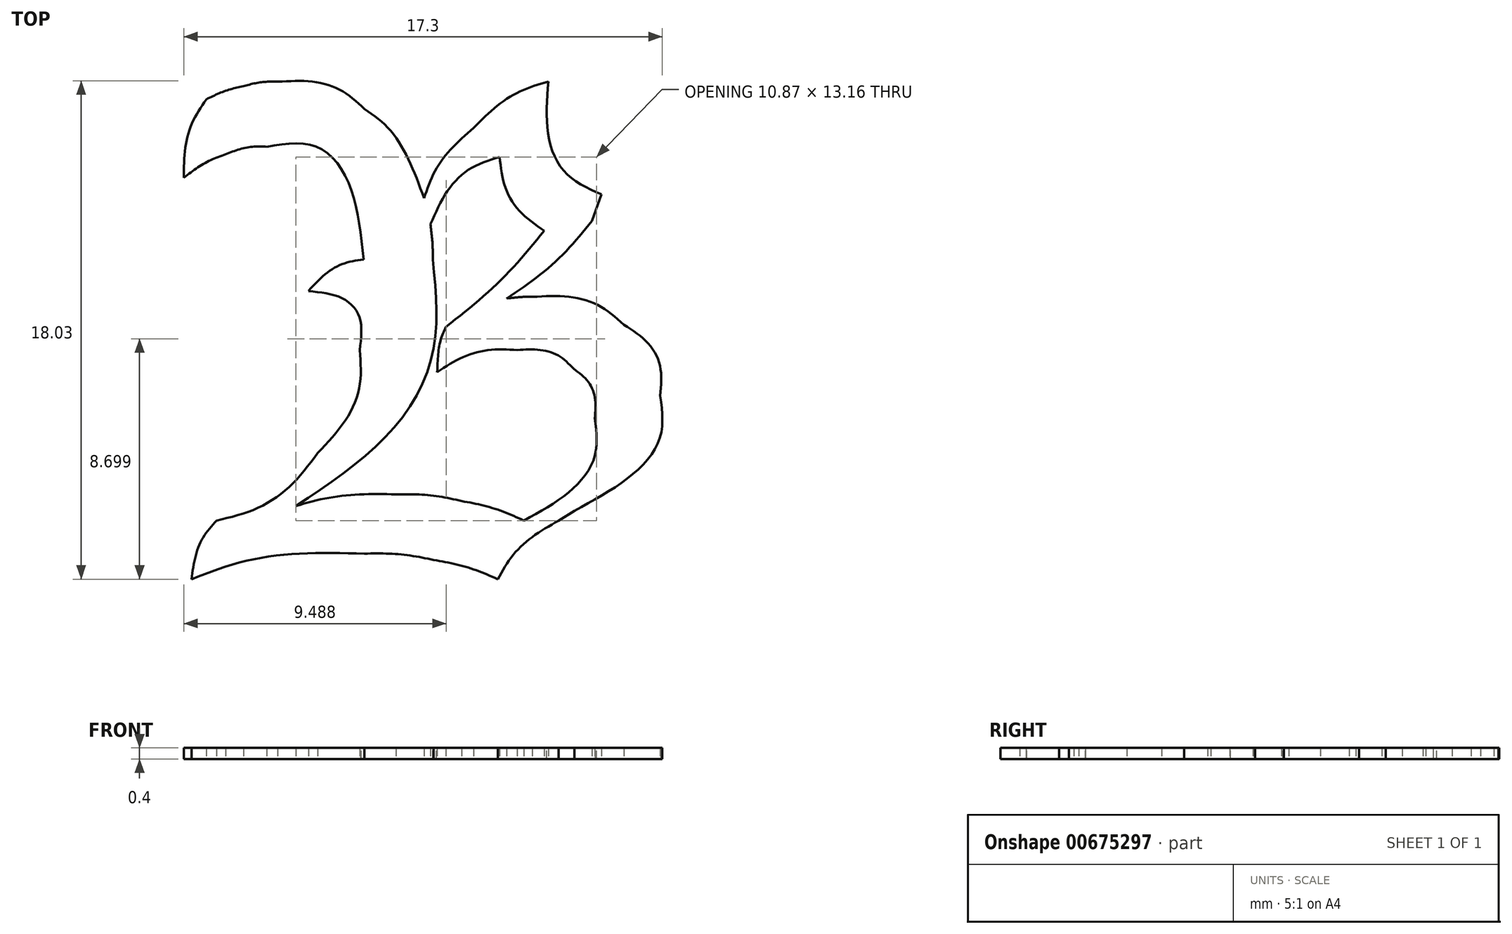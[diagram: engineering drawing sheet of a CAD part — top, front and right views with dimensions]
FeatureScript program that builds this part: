
annotation { "Feature Type Name" : "Feature", "Feature Type Description" : "" }
export const myFeature = defineFeature(function(context is Context, id is Id, definition is map)
    precondition{}
    {
        {
            var Q0;
            Q0=qCreatedBy(makeId("Top.planeOp"),FACE);
            var sketch = newSketch(context, id + "F0", { "sketchPlane" : qUnion([Q0])});
            skFitSpline(sketch, "E0", {"points": [v(-41.57, -9) * mm, v(-41.42, -8.14) * mm, v(-41.12, -7.43) * mm, v(-40.67, -6.88) * mm]});
            skFitSpline(sketch, "E1", {"points": [v(-40.67, -6.88) * mm, v(-39.23, -6.45) * mm, v(-38.01, -5.63) * mm, v(-37, -4.44) * mm]});
            skFitSpline(sketch, "E2", {"points": [v(-37, -4.44) * mm, v(-36, -3.23) * mm, v(-35.49, -1.99) * mm, v(-35.49, -0.7) * mm]});
            skFitSpline(sketch, "E3", {"points": [v(-35.49, -0.7) * mm, v(-35.49, 0.45) * mm, v(-36.1, 1.16) * mm, v(-37.34, 1.42) * mm]});
            skFitSpline(sketch, "E4", {"points": [v(-37.34, 1.42) * mm, v(-36.74, 2.03) * mm, v(-36.08, 2.42) * mm, v(-35.35, 2.57) * mm]});
            skFitSpline(sketch, "E5", {"points": [v(-35.35, 2.57) * mm, v(-35.88, 5.29) * mm, v(-37.04, 6.65) * mm, v(-38.85, 6.65) * mm]});
            skFitSpline(sketch, "E6", {"points": [v(-38.85, 6.65) * mm, v(-39.34, 6.65) * mm, v(-39.84, 6.56) * mm, v(-40.33, 6.37) * mm]});
            skFitSpline(sketch, "E7", {"points": [v(-40.33, 6.37) * mm, v(-40.83, 6.19) * mm, v(-41.34, 5.9) * mm, v(-41.85, 5.53) * mm]});
            skFitSpline(sketch, "E8", {"points": [v(-41.85, 5.53) * mm, v(-41.8, 6.6) * mm, v(-41.52, 7.55) * mm, v(-41.04, 8.36) * mm]});
            skFitSpline(sketch, "E9", {"points": [v(-41.04, 8.36) * mm, v(-40.57, 8.58) * mm, v(-40.13, 8.74) * mm, v(-39.7, 8.84) * mm]});
            skFitSpline(sketch, "E10", {"points": [v(-39.7, 8.84) * mm, v(-39.26, 8.95) * mm, v(-38.85, 9) * mm, v(-38.46, 9) * mm]});
            skFitSpline(sketch, "E11", {"points": [v(-38.46, 9) * mm, v(-37.19, 9) * mm, v(-36.14, 8.67) * mm, v(-35.32, 8.02) * mm]});
            skFitSpline(sketch, "E12", {"points": [v(-35.32, 8.02) * mm, v(-34.49, 7.36) * mm, v(-33.77, 6.28) * mm, v(-33.16, 4.78) * mm]});
            skFitSpline(sketch, "E13", {"points": [v(-33.16, 4.78) * mm, v(-32.8, 5.7) * mm, v(-32.2, 6.54) * mm, v(-31.37, 7.33) * mm]});
            skFitSpline(sketch, "E14", {"points": [v(-31.37, 7.33) * mm, v(-30.52, 8.13) * mm, v(-29.62, 8.68) * mm, v(-28.67, 9) * mm]});
            skFitSpline(sketch, "E15", {"points": [v(-28.67, 9) * mm, v(-28.67, 7.05) * mm, v(-28.03, 5.69) * mm, v(-26.74, 4.92) * mm]});
            skLineSegment(sketch, "E16", {"start": v(-26.74, 4.92) * mm, "end": v(-27.1, 3.96) * mm});
            skFitSpline(sketch, "E17", {"points": [v(-27.1, 3.96) * mm, v(-27.96, 2.93) * mm, v(-29, 2) * mm, v(-30.17, 1.16) * mm]});
            skFitSpline(sketch, "E18", {"points": [v(-30.17, 1.16) * mm, v(-29.81, 1.2) * mm, v(-29.5, 1.22) * mm, v(-29.25, 1.22) * mm]});
            skFitSpline(sketch, "E19", {"points": [v(-29.25, 1.22) * mm, v(-27.9, 1.22) * mm, v(-26.8, 0.88) * mm, v(-25.93, 0.2) * mm]});
            skFitSpline(sketch, "E20", {"points": [v(-25.93, 0.2) * mm, v(-25.06, -0.46) * mm, v(-24.63, -1.32) * mm, v(-24.63, -2.36) * mm]});
            skFitSpline(sketch, "E21", {"points": [v(-24.63, -2.36) * mm, v(-24.63, -3.85) * mm, v(-25.66, -5.24) * mm, v(-27.73, -6.52) * mm]});
            skLineSegment(sketch, "E22", {"start": v(-27.73, -6.52) * mm, "end": v(-28.3, -6.88) * mm});
            skFitSpline(sketch, "E23", {"points": [v(-28.3, -6.88) * mm, v(-29.25, -7.47) * mm, v(-29.99, -8.18) * mm, v(-30.5, -9) * mm]});
            skFitSpline(sketch, "E24", {"points": [v(-30.5, -9) * mm, v(-31.24, -8.7) * mm, v(-32.01, -8.46) * mm, v(-32.81, -8.3) * mm]});
            skFitSpline(sketch, "E25", {"points": [v(-32.81, -8.3) * mm, v(-33.62, -8.15) * mm, v(-34.45, -8.07) * mm, v(-35.32, -8.07) * mm]});
            skFitSpline(sketch, "E26", {"points": [v(-35.32, -8.07) * mm, v(-37.7, -8.07) * mm, v(-39.79, -8.38) * mm, v(-41.57, -9) * mm]});
            skLineSegment(sketch, "E27", {"start": v(-41.57, -9) * mm, "end": v(-41.57, -9) * mm});
            skFitSpline(sketch, "E28", {"points": [v(-37.8, -6.35) * mm, v(-36.7, -6.07) * mm, v(-35.49, -5.93) * mm, v(-34.18, -5.93) * mm]});
            skFitSpline(sketch, "E29", {"points": [v(-34.18, -5.93) * mm, v(-33.37, -5.93) * mm, v(-32.58, -6.01) * mm, v(-31.8, -6.17) * mm]});
            skFitSpline(sketch, "E30", {"points": [v(-31.8, -6.17) * mm, v(-31.03, -6.33) * mm, v(-30.28, -6.56) * mm, v(-29.55, -6.88) * mm]});
            skFitSpline(sketch, "E31", {"points": [v(-29.55, -6.88) * mm, v(-27.84, -5.78) * mm, v(-26.99, -4.54) * mm, v(-26.99, -3.17) * mm]});
            skFitSpline(sketch, "E32", {"points": [v(-26.99, -3.17) * mm, v(-26.99, -2.43) * mm, v(-27.24, -1.84) * mm, v(-27.75, -1.39) * mm]});
            skFitSpline(sketch, "E33", {"points": [v(-27.75, -1.39) * mm, v(-28.26, -0.93) * mm, v(-28.94, -0.7) * mm, v(-29.8, -0.7) * mm]});
            skFitSpline(sketch, "E34", {"points": [v(-29.8, -0.7) * mm, v(-30.81, -0.7) * mm, v(-31.78, -0.97) * mm, v(-32.69, -1.5) * mm]});
            skFitSpline(sketch, "E35", {"points": [v(-32.69, -1.5) * mm, v(-32.65, -0.83) * mm, v(-32.54, -0.28) * mm, v(-32.37, 0.13) * mm]});
            skFitSpline(sketch, "E36", {"points": [v(-32.37, 0.13) * mm, v(-31.05, 1.2) * mm, v(-29.86, 2.37) * mm, v(-28.82, 3.6) * mm]});
            skFitSpline(sketch, "E37", {"points": [v(-28.82, 3.6) * mm, v(-29.7, 4.31) * mm, v(-30.24, 5.2) * mm, v(-30.43, 6.28) * mm]});
            skFitSpline(sketch, "E38", {"points": [v(-30.43, 6.28) * mm, v(-31.48, 5.86) * mm, v(-32.31, 5.05) * mm, v(-32.93, 3.85) * mm]});
            skFitSpline(sketch, "E39", {"points": [v(-32.93, 3.85) * mm, v(-32.88, 3.36) * mm, v(-32.85, 2.93) * mm, v(-32.85, 2.57) * mm]});
            skFitSpline(sketch, "E40", {"points": [v(-32.85, 2.57) * mm, v(-32.85, -0.82) * mm, v(-34.5, -3.8) * mm, v(-37.8, -6.35) * mm]});
            skFitSpline(sketch, "E41", {"points": [v(-23.24, -4.97) * mm, v(-23.24, -5.33) * mm, v(-23.18, -5.74) * mm, v(-23.07, -6.2) * mm]});
            skFitSpline(sketch, "E42", {"points": [v(-23.07, -6.2) * mm, v(-22.94, -6.64) * mm, v(-22.77, -7.06) * mm, v(-22.55, -7.46) * mm]});
            skFitSpline(sketch, "E43", {"points": [v(-22.55, -7.46) * mm, v(-22.31, -7.85) * mm, v(-22.03, -8.18) * mm, v(-21.72, -8.45) * mm]});
            skFitSpline(sketch, "E44", {"points": [v(-21.72, -8.45) * mm, v(-21.4, -8.72) * mm, v(-21.05, -8.86) * mm, v(-20.65, -8.86) * mm]});
            skFitSpline(sketch, "E45", {"points": [v(-20.65, -8.86) * mm, v(-20.16, -8.86) * mm, v(-19.64, -8.73) * mm, v(-19.08, -8.48) * mm]});
            skFitSpline(sketch, "E46", {"points": [v(-19.08, -8.48) * mm, v(-18.53, -8.22) * mm, v(-18.03, -7.95) * mm, v(-17.59, -7.65) * mm]});
            skFitSpline(sketch, "E47", {"points": [v(-17.59, -7.65) * mm, v(-17.13, -7.35) * mm, v(-16.78, -7.08) * mm, v(-16.52, -6.84) * mm]});
            skFitSpline(sketch, "E48", {"points": [v(-16.52, -6.84) * mm, v(-16.25, -6.59) * mm, v(-16.17, -6.48) * mm, v(-16.26, -6.5) * mm]});
            skFitSpline(sketch, "E49", {"points": [v(-16.26, -6.5) * mm, v(-16.37, -6.54) * mm, v(-16.53, -6.62) * mm, v(-16.74, -6.74) * mm]});
            skFitSpline(sketch, "E50", {"points": [v(-16.74, -6.74) * mm, v(-16.94, -6.87) * mm, v(-17.16, -7) * mm, v(-17.4, -7.15) * mm]});
            skFitSpline(sketch, "E51", {"points": [v(-17.4, -7.15) * mm, v(-17.64, -7.3) * mm, v(-17.87, -7.42) * mm, v(-18.11, -7.53) * mm]});
            skFitSpline(sketch, "E52", {"points": [v(-18.11, -7.53) * mm, v(-18.35, -7.64) * mm, v(-18.56, -7.7) * mm, v(-18.75, -7.7) * mm]});
            skFitSpline(sketch, "E53", {"points": [v(-18.75, -7.7) * mm, v(-19.08, -7.7) * mm, v(-19.38, -7.58) * mm, v(-19.65, -7.34) * mm]});
            skFitSpline(sketch, "E54", {"points": [v(-19.65, -7.34) * mm, v(-19.9, -7.08) * mm, v(-20.13, -6.8) * mm, v(-20.32, -6.46) * mm]});
            skFitSpline(sketch, "E55", {"points": [v(-20.32, -6.46) * mm, v(-20.5, -6.13) * mm, v(-20.63, -5.8) * mm, v(-20.72, -5.49) * mm]});
            skFitSpline(sketch, "E56", {"points": [v(-20.72, -5.49) * mm, v(-20.82, -5.16) * mm, v(-20.86, -4.91) * mm, v(-20.86, -4.75) * mm]});
            skFitSpline(sketch, "E57", {"points": [v(-20.86, -4.75) * mm, v(-20.83, -4.75) * mm, v(-20.67, -4.7) * mm, v(-20.37, -4.59) * mm]});
            skFitSpline(sketch, "E58", {"points": [v(-20.37, -4.59) * mm, v(-20.06, -4.46) * mm, v(-19.7, -4.3) * mm, v(-19.27, -4.14) * mm]});
            skFitSpline(sketch, "E59", {"points": [v(-19.27, -4.14) * mm, v(-18.83, -3.95) * mm, v(-18.36, -3.74) * mm, v(-17.85, -3.52) * mm]});
            skFitSpline(sketch, "E60", {"points": [v(-17.85, -3.52) * mm, v(-17.34, -3.28) * mm, v(-16.89, -3.05) * mm, v(-16.47, -2.83) * mm]});
            skFitSpline(sketch, "E61", {"points": [v(-16.47, -2.83) * mm, v(-16.05, -2.6) * mm, v(-15.7, -2.4) * mm, v(-15.4, -2.21) * mm]});
            skFitSpline(sketch, "E62", {"points": [v(-15.4, -2.21) * mm, v(-15.12, -2.02) * mm, v(-14.98, -1.88) * mm, v(-14.98, -1.79) * mm]});
            skFitSpline(sketch, "E63", {"points": [v(-14.98, -1.79) * mm, v(-14.98, -1.68) * mm, v(-15.07, -1.48) * mm, v(-15.24, -1.2) * mm]});
            skFitSpline(sketch, "E64", {"points": [v(-15.24, -1.2) * mm, v(-15.4, -0.9) * mm, v(-15.61, -0.62) * mm, v(-15.88, -0.34) * mm]});
            skFitSpline(sketch, "E65", {"points": [v(-15.88, -0.34) * mm, v(-16.13, -0.04) * mm, v(-16.43, 0.22) * mm, v(-16.76, 0.44) * mm]});
            skFitSpline(sketch, "E66", {"points": [v(-16.76, 0.44) * mm, v(-17.08, 0.66) * mm, v(-17.4, 0.78) * mm, v(-17.73, 0.78) * mm]});
            skFitSpline(sketch, "E67", {"points": [v(-17.73, 0.78) * mm, v(-18.2, 0.78) * mm, v(-18.74, 0.62) * mm, v(-19.37, 0.32) * mm]});
            skFitSpline(sketch, "E68", {"points": [v(-19.37, 0.32) * mm, v(-19.99, 0.02) * mm, v(-20.59, -0.39) * mm, v(-21.17, -0.9) * mm]});
            skFitSpline(sketch, "E69", {"points": [v(-21.17, -0.9) * mm, v(-21.74, -1.42) * mm, v(-22.23, -2.02) * mm, v(-22.64, -2.71) * mm]});
            skFitSpline(sketch, "E70", {"points": [v(-22.64, -2.71) * mm, v(-23.04, -3.4) * mm, v(-23.24, -4.16) * mm, v(-23.24, -4.97) * mm]});
            skFitSpline(sketch, "E71", {"points": [v(-20.91, -4.37) * mm, v(-20.96, -3.74) * mm, v(-20.92, -3.17) * mm, v(-20.8, -2.66) * mm]});
            skFitSpline(sketch, "E72", {"points": [v(-20.8, -2.66) * mm, v(-20.67, -2.16) * mm, v(-20.5, -1.72) * mm, v(-20.32, -1.36) * mm]});
            skFitSpline(sketch, "E73", {"points": [v(-20.32, -1.36) * mm, v(-20.13, -1) * mm, v(-19.93, -0.72) * mm, v(-19.72, -0.53) * mm]});
            skFitSpline(sketch, "E74", {"points": [v(-19.72, -0.53) * mm, v(-19.5, -0.32) * mm, v(-19.32, -0.22) * mm, v(-19.18, -0.22) * mm]});
            skFitSpline(sketch, "E75", {"points": [v(-19.18, -0.22) * mm, v(-19.04, -0.22) * mm, v(-18.86, -0.32) * mm, v(-18.66, -0.53) * mm]});
            skFitSpline(sketch, "E76", {"points": [v(-18.66, -0.53) * mm, v(-18.44, -0.72) * mm, v(-18.23, -0.95) * mm, v(-18.04, -1.22) * mm]});
            skFitSpline(sketch, "E77", {"points": [v(-18.04, -1.22) * mm, v(-17.85, -1.49) * mm, v(-17.7, -1.76) * mm, v(-17.61, -2.05) * mm]});
            skFitSpline(sketch, "E78", {"points": [v(-17.61, -2.05) * mm, v(-17.5, -2.32) * mm, v(-17.5, -2.53) * mm, v(-17.61, -2.69) * mm]});
            skFitSpline(sketch, "E79", {"points": [v(-17.61, -2.69) * mm, v(-17.74, -2.88) * mm, v(-17.99, -3.08) * mm, v(-18.35, -3.28) * mm]});
            skFitSpline(sketch, "E80", {"points": [v(-18.35, -3.28) * mm, v(-18.71, -3.49) * mm, v(-19.08, -3.68) * mm, v(-19.46, -3.85) * mm]});
            skFitSpline(sketch, "E81", {"points": [v(-19.46, -3.85) * mm, v(-19.84, -4) * mm, v(-20.18, -4.14) * mm, v(-20.48, -4.23) * mm]});
            skFitSpline(sketch, "E82", {"points": [v(-20.48, -4.23) * mm, v(-20.77, -4.33) * mm, v(-20.91, -4.37) * mm, v(-20.91, -4.37) * mm, v(-20.48, -4.23) * mm]});
            skFitSpline(sketch, "E83", {"points": [v(-13.43, -7.1) * mm, v(-13.54, -7.56) * mm, v(-13.43, -7.95) * mm, v(-13.1, -8.26) * mm]});
            skFitSpline(sketch, "E84", {"points": [v(-13.1, -8.26) * mm, v(-12.77, -8.56) * mm, v(-12.3, -8.75) * mm, v(-11.72, -8.8) * mm]});
            skFitSpline(sketch, "E85", {"points": [v(-11.72, -8.8) * mm, v(-11.12, -8.87) * mm, v(-10.45, -8.8) * mm, v(-9.7, -8.57) * mm]});
            skFitSpline(sketch, "E86", {"points": [v(-9.7, -8.57) * mm, v(-8.95, -8.35) * mm, v(-8.2, -7.94) * mm, v(-7.48, -7.34) * mm]});
            skFitSpline(sketch, "E87", {"points": [v(-7.48, -7.34) * mm, v(-7.38, -7.26) * mm, v(-7.42, -7.25) * mm, v(-7.6, -7.31) * mm]});
            skFitSpline(sketch, "E88", {"points": [v(-7.6, -7.31) * mm, v(-7.76, -7.38) * mm, v(-8, -7.44) * mm, v(-8.3, -7.5) * mm]});
            skFitSpline(sketch, "E89", {"points": [v(-8.3, -7.5) * mm, v(-8.62, -7.55) * mm, v(-8.98, -7.57) * mm, v(-9.38, -7.55) * mm]});
            skFitSpline(sketch, "E90", {"points": [v(-9.38, -7.55) * mm, v(-9.77, -7.52) * mm, v(-10.14, -7.39) * mm, v(-10.47, -7.15) * mm]});
            skFitSpline(sketch, "E91", {"points": [v(-10.47, -7.15) * mm, v(-10.83, -6.9) * mm, v(-11.05, -6.45) * mm, v(-11.13, -5.82) * mm]});
            skFitSpline(sketch, "E92", {"points": [v(-11.13, -5.82) * mm, v(-11.21, -5.17) * mm, v(-11.2, -4.42) * mm, v(-11.08, -3.57) * mm]});
            skFitSpline(sketch, "E93", {"points": [v(-11.08, -3.57) * mm, v(-10.97, -2.7) * mm, v(-10.8, -1.77) * mm, v(-10.54, -0.8) * mm]});
            skFitSpline(sketch, "E94", {"points": [v(-10.54, -0.8) * mm, v(-10.29, 0.2) * mm, v(-10, 1.18) * mm, v(-9.7, 2.13) * mm]});
            skFitSpline(sketch, "E95", {"points": [v(-9.7, 2.13) * mm, v(-9.4, 3.08) * mm, v(-9.1, 3.95) * mm, v(-8.78, 4.76) * mm]});
            skFitSpline(sketch, "E96", {"points": [v(-8.78, 4.76) * mm, v(-8.47, 5.58) * mm, v(-8.19, 6.25) * mm, v(-7.95, 6.78) * mm]});
            skFitSpline(sketch, "E97", {"points": [v(-7.95, 6.78) * mm, v(-7.81, 7.1) * mm, v(-7.66, 7.36) * mm, v(-7.5, 7.58) * mm]});
            skFitSpline(sketch, "E98", {"points": [v(-7.5, 7.58) * mm, v(-7.33, 7.8) * mm, v(-7.19, 7.99) * mm, v(-7.08, 8.13) * mm]});
            skFitSpline(sketch, "E99", {"points": [v(-7.08, 8.13) * mm, v(-6.96, 8.27) * mm, v(-6.9, 8.37) * mm, v(-6.86, 8.41) * mm]});
            skFitSpline(sketch, "E100", {"points": [v(-6.86, 8.41) * mm, v(-6.83, 8.48) * mm, v(-6.88, 8.5) * mm, v(-7, 8.46) * mm]});
            skFitSpline(sketch, "E101", {"points": [v(-7, 8.46) * mm, v(-7.2, 8.41) * mm, v(-7.49, 8.36) * mm, v(-7.83, 8.3) * mm]});
            skFitSpline(sketch, "E102", {"points": [v(-7.83, 8.3) * mm, v(-8.18, 8.25) * mm, v(-8.52, 8.2) * mm, v(-8.85, 8.15) * mm]});
            skFitSpline(sketch, "E103", {"points": [v(-8.85, 8.15) * mm, v(-9.19, 8.12) * mm, v(-9.48, 8.09) * mm, v(-9.73, 8.06) * mm]});
            skFitSpline(sketch, "E104", {"points": [v(-9.73, 8.06) * mm, v(-9.97, 8.04) * mm, v(-10.09, 8.03) * mm, v(-10.09, 8.03) * mm, v(-9.73, 8.06) * mm]});
            skFitSpline(sketch, "E105", {"points": [v(-10.09, 8.03) * mm, v(-10.36, 7.27) * mm, v(-10.63, 6.3) * mm, v(-10.9, 5.12) * mm]});
            skFitSpline(sketch, "E106", {"points": [v(-10.9, 5.12) * mm, v(-11.15, 3.93) * mm, v(-11.42, 2.65) * mm, v(-11.7, 1.27) * mm]});
            skFitSpline(sketch, "E107", {"points": [v(-11.7, 1.27) * mm, v(-11.97, -0.1) * mm, v(-12.25, -1.52) * mm, v(-12.53, -2.97) * mm]});
            skFitSpline(sketch, "E108", {"points": [v(-12.53, -2.97) * mm, v(-12.82, -4.43) * mm, v(-13.12, -5.8) * mm, v(-13.43, -7.1) * mm]});
            skFitSpline(sketch, "E109", {"points": [v(-6.3, -7.1) * mm, v(-6.4, -7.56) * mm, v(-6.3, -7.95) * mm, v(-5.97, -8.26) * mm]});
            skFitSpline(sketch, "E110", {"points": [v(-5.97, -8.26) * mm, v(-5.63, -8.56) * mm, v(-5.17, -8.75) * mm, v(-4.59, -8.8) * mm]});
            skFitSpline(sketch, "E111", {"points": [v(-4.59, -8.8) * mm, v(-3.99, -8.87) * mm, v(-3.32, -8.8) * mm, v(-2.57, -8.57) * mm]});
            skFitSpline(sketch, "E112", {"points": [v(-2.57, -8.57) * mm, v(-1.81, -8.35) * mm, v(-1.07, -7.94) * mm, v(-0.34, -7.34) * mm]});
            skFitSpline(sketch, "E113", {"points": [v(-0.34, -7.34) * mm, v(-0.25, -7.26) * mm, v(-0.29, -7.25) * mm, v(-0.46, -7.31) * mm]});
            skFitSpline(sketch, "E114", {"points": [v(-0.46, -7.31) * mm, v(-0.62, -7.38) * mm, v(-0.86, -7.44) * mm, v(-1.17, -7.5) * mm]});
            skFitSpline(sketch, "E115", {"points": [v(-1.17, -7.5) * mm, v(-1.49, -7.55) * mm, v(-1.85, -7.57) * mm, v(-2.24, -7.55) * mm]});
            skFitSpline(sketch, "E116", {"points": [v(-2.24, -7.55) * mm, v(-2.64, -7.52) * mm, v(-3, -7.39) * mm, v(-3.33, -7.15) * mm]});
            skFitSpline(sketch, "E117", {"points": [v(-3.33, -7.15) * mm, v(-3.7, -6.9) * mm, v(-3.92, -6.45) * mm, v(-4, -5.82) * mm]});
            skFitSpline(sketch, "E118", {"points": [v(-4, -5.82) * mm, v(-4.08, -5.17) * mm, v(-4.06, -4.42) * mm, v(-3.95, -3.57) * mm]});
            skFitSpline(sketch, "E119", {"points": [v(-3.95, -3.57) * mm, v(-3.84, -2.7) * mm, v(-3.66, -1.77) * mm, v(-3.4, -0.8) * mm]});
            skFitSpline(sketch, "E120", {"points": [v(-3.4, -0.8) * mm, v(-3.15, 0.2) * mm, v(-2.87, 1.18) * mm, v(-2.57, 2.13) * mm]});
            skFitSpline(sketch, "E121", {"points": [v(-2.57, 2.13) * mm, v(-2.27, 3.08) * mm, v(-1.96, 3.95) * mm, v(-1.65, 4.76) * mm]});
            skFitSpline(sketch, "E122", {"points": [v(-1.65, 4.76) * mm, v(-1.33, 5.58) * mm, v(-1.05, 6.25) * mm, v(-0.82, 6.78) * mm]});
            skFitSpline(sketch, "E123", {"points": [v(-0.82, 6.78) * mm, v(-0.68, 7.1) * mm, v(-0.53, 7.36) * mm, v(-0.37, 7.58) * mm]});
            skFitSpline(sketch, "E124", {"points": [v(-0.37, 7.58) * mm, v(-0.2, 7.8) * mm, v(-0.05, 7.99) * mm, v(0.06, 8.13) * mm]});
            skFitSpline(sketch, "E125", {"points": [v(0.06, 8.13) * mm, v(0.17, 8.27) * mm, v(0.24, 8.37) * mm, v(0.27, 8.41) * mm]});
            skFitSpline(sketch, "E126", {"points": [v(0.27, 8.41) * mm, v(0.3, 8.48) * mm, v(0.26, 8.5) * mm, v(0.13, 8.46) * mm]});
            skFitSpline(sketch, "E127", {"points": [v(0.13, 8.46) * mm, v(-0.07, 8.41) * mm, v(-0.35, 8.36) * mm, v(-0.7, 8.3) * mm]});
            skFitSpline(sketch, "E128", {"points": [v(-0.7, 8.3) * mm, v(-1.05, 8.25) * mm, v(-1.39, 8.2) * mm, v(-1.72, 8.15) * mm]});
            skFitSpline(sketch, "E129", {"points": [v(-1.72, 8.15) * mm, v(-2.05, 8.12) * mm, v(-2.34, 8.09) * mm, v(-2.6, 8.06) * mm]});
            skFitSpline(sketch, "E130", {"points": [v(-2.6, 8.06) * mm, v(-2.83, 8.04) * mm, v(-2.95, 8.03) * mm, v(-2.95, 8.03) * mm, v(-2.6, 8.06) * mm]});
            skFitSpline(sketch, "E131", {"points": [v(-2.95, 8.03) * mm, v(-3.22, 7.27) * mm, v(-3.5, 6.3) * mm, v(-3.76, 5.12) * mm]});
            skFitSpline(sketch, "E132", {"points": [v(-3.76, 5.12) * mm, v(-4.01, 3.93) * mm, v(-4.28, 2.65) * mm, v(-4.57, 1.27) * mm]});
            skFitSpline(sketch, "E133", {"points": [v(-4.57, 1.27) * mm, v(-4.83, -0.1) * mm, v(-5.11, -1.52) * mm, v(-5.4, -2.97) * mm]});
            skFitSpline(sketch, "E134", {"points": [v(-5.4, -2.97) * mm, v(-5.68, -4.43) * mm, v(-5.98, -5.8) * mm, v(-6.3, -7.1) * mm]});
            skFitSpline(sketch, "E135", {"points": [v(0.32, -8.12) * mm, v(0.32, -8.36) * mm, v(0.43, -8.5) * mm, v(0.65, -8.57) * mm]});
            skFitSpline(sketch, "E136", {"points": [v(0.65, -8.57) * mm, v(0.89, -8.65) * mm, v(1.16, -8.67) * mm, v(1.48, -8.62) * mm]});
            skFitSpline(sketch, "E137", {"points": [v(1.48, -8.62) * mm, v(1.81, -8.59) * mm, v(2.15, -8.52) * mm, v(2.5, -8.4) * mm]});
            skFitSpline(sketch, "E138", {"points": [v(2.5, -8.4) * mm, v(2.85, -8.28) * mm, v(3.14, -8.15) * mm, v(3.38, -8.03) * mm]});
            skFitSpline(sketch, "E139", {"points": [v(3.38, -8.03) * mm, v(3.77, -7.79) * mm, v(4.18, -7.46) * mm, v(4.6, -7.03) * mm]});
            skFitSpline(sketch, "E140", {"points": [v(4.6, -7.03) * mm, v(5.05, -6.59) * mm, v(5.45, -6.17) * mm, v(5.8, -5.77) * mm]});
            skFitSpline(sketch, "E141", {"points": [v(5.8, -5.77) * mm, v(6.14, -5.36) * mm, v(6.43, -5.03) * mm, v(6.65, -4.78) * mm]});
            skFitSpline(sketch, "E142", {"points": [v(6.65, -4.78) * mm, v(6.87, -4.52) * mm, v(6.97, -4.47) * mm, v(6.96, -4.6) * mm]});
            skLineSegment(sketch, "E143", {"start": v(6.96, -4.6) * mm, "end": v(6.37, -8.4) * mm});
            skFitSpline(sketch, "E144", {"points": [v(6.37, -8.4) * mm, v(6.35, -8.52) * mm, v(6.48, -8.58) * mm, v(6.74, -8.6) * mm]});
            skFitSpline(sketch, "E145", {"points": [v(6.74, -8.6) * mm, v(7.01, -8.61) * mm, v(7.33, -8.6) * mm, v(7.7, -8.55) * mm]});
            skFitSpline(sketch, "E146", {"points": [v(7.7, -8.55) * mm, v(8.07, -8.5) * mm, v(8.45, -8.44) * mm, v(8.83, -8.38) * mm]});
            skFitSpline(sketch, "E147", {"points": [v(8.83, -8.38) * mm, v(9.23, -8.3) * mm, v(9.54, -8.23) * mm, v(9.78, -8.17) * mm]});
            skFitSpline(sketch, "E148", {"points": [v(9.78, -8.17) * mm, v(10.02, -8.09) * mm, v(10.13, -8.04) * mm, v(10.11, -8.03) * mm]});
            skFitSpline(sketch, "E149", {"points": [v(10.11, -8.03) * mm, v(10.11, -8) * mm, v(9.9, -8) * mm, v(9.47, -8.05) * mm]});
            skFitSpline(sketch, "E150", {"points": [v(9.47, -8.05) * mm, v(9.27, -8.08) * mm, v(9.1, -8.03) * mm, v(9, -7.88) * mm]});
            skFitSpline(sketch, "E151", {"points": [v(9, -7.88) * mm, v(8.89, -7.73) * mm, v(8.8, -7.54) * mm, v(8.76, -7.34) * mm]});
            skFitSpline(sketch, "E152", {"points": [v(8.76, -7.34) * mm, v(8.71, -7.13) * mm, v(8.68, -6.92) * mm, v(8.67, -6.7) * mm]});
            skFitSpline(sketch, "E153", {"points": [v(8.67, -6.7) * mm, v(8.67, -6.46) * mm, v(8.67, -6.27) * mm, v(8.67, -6.13) * mm]});
            skFitSpline(sketch, "E154", {"points": [v(8.67, -6.13) * mm, v(8.67, -5.34) * mm, v(8.74, -4.55) * mm, v(8.88, -3.76) * mm]});
            skFitSpline(sketch, "E155", {"points": [v(8.88, -3.76) * mm, v(9.02, -2.97) * mm, v(9.2, -2.25) * mm, v(9.4, -1.6) * mm]});
            skFitSpline(sketch, "E156", {"points": [v(9.4, -1.6) * mm, v(9.6, -0.93) * mm, v(9.83, -0.38) * mm, v(10.07, 0.06) * mm]});
            skFitSpline(sketch, "E157", {"points": [v(10.07, 0.06) * mm, v(10.3, 0.52) * mm, v(10.5, 0.81) * mm, v(10.68, 0.94) * mm]});
            skFitSpline(sketch, "E158", {"points": [v(10.68, 0.94) * mm, v(10.54, 0.94) * mm, v(10.18, 0.86) * mm, v(9.61, 0.7) * mm]});
            skFitSpline(sketch, "E159", {"points": [v(9.61, 0.7) * mm, v(9.06, 0.56) * mm, v(8.4, 0.33) * mm, v(7.62, 0.02) * mm]});
            skFitSpline(sketch, "E160", {"points": [v(7.62, 0.02) * mm, v(6.86, -0.28) * mm, v(6.05, -0.68) * mm, v(5.18, -1.17) * mm]});
            skFitSpline(sketch, "E161", {"points": [v(5.18, -1.17) * mm, v(4.32, -1.66) * mm, v(3.53, -2.25) * mm, v(2.8, -2.93) * mm]});
            skFitSpline(sketch, "E162", {"points": [v(2.8, -2.93) * mm, v(2.1, -3.59) * mm, v(1.5, -4.36) * mm, v(1.03, -5.23) * mm]});
            skFitSpline(sketch, "E163", {"points": [v(1.03, -5.23) * mm, v(0.55, -6.08) * mm, v(0.32, -7.05) * mm, v(0.32, -8.12) * mm]});
            skFitSpline(sketch, "E164", {"points": [v(2.71, -7.12) * mm, v(2.71, -6.3) * mm, v(2.81, -5.57) * mm, v(3.02, -4.94) * mm]});
            skFitSpline(sketch, "E165", {"points": [v(3.02, -4.94) * mm, v(3.24, -4.3) * mm, v(3.52, -3.72) * mm, v(3.85, -3.23) * mm]});
            skFitSpline(sketch, "E166", {"points": [v(3.85, -3.23) * mm, v(4.18, -2.74) * mm, v(4.55, -2.33) * mm, v(4.94, -2) * mm]});
            skFitSpline(sketch, "E167", {"points": [v(4.94, -2) * mm, v(5.35, -1.65) * mm, v(5.74, -1.38) * mm, v(6.1, -1.17) * mm]});
            skFitSpline(sketch, "E168", {"points": [v(6.1, -1.17) * mm, v(6.47, -0.95) * mm, v(6.78, -0.8) * mm, v(7.05, -0.7) * mm]});
            skFitSpline(sketch, "E169", {"points": [v(7.05, -0.7) * mm, v(7.34, -0.6) * mm, v(7.53, -0.55) * mm, v(7.62, -0.55) * mm]});
            skLineSegment(sketch, "E170", {"start": v(7.62, -0.55) * mm, "end": v(7.17, -3.45) * mm});
            skFitSpline(sketch, "E171", {"points": [v(7.17, -3.45) * mm, v(7.03, -3.7) * mm, v(6.82, -4) * mm, v(6.55, -4.35) * mm]});
            skFitSpline(sketch, "E172", {"points": [v(6.55, -4.35) * mm, v(6.29, -4.7) * mm, v(5.99, -5.05) * mm, v(5.65, -5.42) * mm]});
            skFitSpline(sketch, "E173", {"points": [v(5.65, -5.42) * mm, v(5.32, -5.78) * mm, v(4.98, -6.13) * mm, v(4.63, -6.46) * mm]});
            skFitSpline(sketch, "E174", {"points": [v(4.63, -6.46) * mm, v(4.29, -6.8) * mm, v(3.97, -7.05) * mm, v(3.68, -7.24) * mm]});
            skFitSpline(sketch, "E175", {"points": [v(3.68, -7.24) * mm, v(3.4, -7.43) * mm, v(3.16, -7.53) * mm, v(2.97, -7.53) * mm]});
            skFitSpline(sketch, "E176", {"points": [v(2.97, -7.53) * mm, v(2.8, -7.53) * mm, v(2.71, -7.4) * mm, v(2.71, -7.12) * mm]});
            skFitSpline(sketch, "E177", {"points": [v(12.57, -5.9) * mm, v(12.45, -6.35) * mm, v(12.45, -6.77) * mm, v(12.6, -7.15) * mm]});
            skFitSpline(sketch, "E178", {"points": [v(12.6, -7.15) * mm, v(12.75, -7.51) * mm, v(13, -7.82) * mm, v(13.36, -8.07) * mm]});
            skFitSpline(sketch, "E179", {"points": [v(13.36, -8.07) * mm, v(13.7, -8.31) * mm, v(14.13, -8.48) * mm, v(14.64, -8.6) * mm]});
            skFitSpline(sketch, "E180", {"points": [v(14.64, -8.6) * mm, v(15.14, -8.7) * mm, v(15.69, -8.73) * mm, v(16.27, -8.67) * mm]});
            skFitSpline(sketch, "E181", {"points": [v(16.27, -8.67) * mm, v(16.86, -8.62) * mm, v(17.46, -8.48) * mm, v(18.08, -8.24) * mm]});
            skFitSpline(sketch, "E182", {"points": [v(18.08, -8.24) * mm, v(18.7, -7.99) * mm, v(19.31, -7.63) * mm, v(19.88, -7.17) * mm]});
            skFitSpline(sketch, "E183", {"points": [v(19.88, -7.17) * mm, v(19.9, -7.16) * mm, v(19.8, -7.2) * mm, v(19.57, -7.3) * mm]});
            skFitSpline(sketch, "E184", {"points": [v(19.57, -7.3) * mm, v(19.35, -7.37) * mm, v(19.05, -7.44) * mm, v(18.67, -7.5) * mm]});
            skFitSpline(sketch, "E185", {"points": [v(18.67, -7.5) * mm, v(18.3, -7.55) * mm, v(17.88, -7.55) * mm, v(17.39, -7.5) * mm]});
            skFitSpline(sketch, "E186", {"points": [v(17.39, -7.5) * mm, v(16.91, -7.46) * mm, v(16.42, -7.3) * mm, v(15.92, -7) * mm]});
            skFitSpline(sketch, "E187", {"points": [v(15.92, -7) * mm, v(15.32, -6.67) * mm, v(14.97, -6.24) * mm, v(14.87, -5.7) * mm]});
            skFitSpline(sketch, "E188", {"points": [v(14.87, -5.7) * mm, v(14.78, -5.16) * mm, v(14.81, -4.59) * mm, v(14.97, -3.97) * mm]});
            skFitSpline(sketch, "E189", {"points": [v(14.97, -3.97) * mm, v(15.13, -3.35) * mm, v(15.35, -2.73) * mm, v(15.63, -2.1) * mm]});
            skFitSpline(sketch, "E190", {"points": [v(15.63, -2.1) * mm, v(15.92, -1.46) * mm, v(16.15, -0.89) * mm, v(16.32, -0.36) * mm]});
            skFitSpline(sketch, "E191", {"points": [v(16.32, -0.36) * mm, v(16.32, -0.36) * mm, v(16.47, -0.34) * mm, v(16.77, -0.3) * mm, v(16.32, -0.36) * mm]});
            skFitSpline(sketch, "E192", {"points": [v(16.77, -0.3) * mm, v(17.07, -0.23) * mm, v(17.45, -0.15) * mm, v(17.91, -0.06) * mm]});
            skFitSpline(sketch, "E193", {"points": [v(17.91, -0.06) * mm, v(18.37, 0.06) * mm, v(18.88, 0.19) * mm, v(19.43, 0.35) * mm]});
            skFitSpline(sketch, "E194", {"points": [v(19.43, 0.35) * mm, v(19.98, 0.5) * mm, v(20.51, 0.7) * mm, v(21.02, 0.92) * mm]});
            skFitSpline(sketch, "E195", {"points": [v(21.02, 0.92) * mm, v(21, 0.92) * mm, v(20.88, 0.9) * mm, v(20.66, 0.87) * mm]});
            skFitSpline(sketch, "E196", {"points": [v(20.66, 0.87) * mm, v(20.44, 0.85) * mm, v(20.14, 0.83) * mm, v(19.76, 0.8) * mm]});
            skFitSpline(sketch, "E197", {"points": [v(19.76, 0.8) * mm, v(19.4, 0.78) * mm, v(19.03, 0.77) * mm, v(18.65, 0.75) * mm]});
            skFitSpline(sketch, "E198", {"points": [v(18.65, 0.75) * mm, v(18.27, 0.74) * mm, v(17.9, 0.72) * mm, v(17.55, 0.7) * mm]});
            skFitSpline(sketch, "E199", {"points": [v(17.55, 0.7) * mm, v(17.22, 0.7) * mm, v(16.97, 0.72) * mm, v(16.8, 0.75) * mm]});
            skFitSpline(sketch, "E200", {"points": [v(16.8, 0.75) * mm, v(16.81, 0.77) * mm, v(16.87, 0.85) * mm, v(16.96, 1.01) * mm]});
            skFitSpline(sketch, "E201", {"points": [v(16.96, 1.01) * mm, v(17.06, 1.19) * mm, v(17.2, 1.42) * mm, v(17.36, 1.7) * mm]});
            skFitSpline(sketch, "E202", {"points": [v(17.36, 1.7) * mm, v(17.55, 2) * mm, v(17.75, 2.3) * mm, v(17.96, 2.58) * mm]});
            skFitSpline(sketch, "E203", {"points": [v(17.96, 2.58) * mm, v(18, 2.64) * mm, v(17.94, 2.65) * mm, v(17.77, 2.6) * mm]});
            skFitSpline(sketch, "E204", {"points": [v(17.77, 2.6) * mm, v(17.61, 2.57) * mm, v(17.39, 2.52) * mm, v(17.1, 2.46) * mm]});
            skFitSpline(sketch, "E205", {"points": [v(17.1, 2.46) * mm, v(16.82, 2.4) * mm, v(16.48, 2.33) * mm, v(16.08, 2.27) * mm]});
            skFitSpline(sketch, "E206", {"points": [v(16.08, 2.27) * mm, v(15.7, 2.2) * mm, v(15.3, 2.17) * mm, v(14.9, 2.17) * mm]});
            skFitSpline(sketch, "E207", {"points": [v(14.9, 2.17) * mm, v(14.9, 2.16) * mm, v(14.88, 2.08) * mm, v(14.85, 1.94) * mm]});
            skFitSpline(sketch, "E208", {"points": [v(14.85, 1.94) * mm, v(14.82, 1.81) * mm, v(14.77, 1.64) * mm, v(14.7, 1.44) * mm]});
            skFitSpline(sketch, "E209", {"points": [v(14.7, 1.44) * mm, v(14.66, 1.23) * mm, v(14.61, 1.06) * mm, v(14.57, 0.92) * mm]});
            skFitSpline(sketch, "E210", {"points": [v(14.57, 0.92) * mm, v(14.55, 0.92) * mm, v(14.5, 0.92) * mm, v(14.4, 0.92) * mm]});
            skFitSpline(sketch, "E211", {"points": [v(14.4, 0.92) * mm, v(14.32, 0.93) * mm, v(14.23, 0.94) * mm, v(14.12, 0.94) * mm]});
            skFitSpline(sketch, "E212", {"points": [v(14.12, 0.94) * mm, v(14, 0.96) * mm, v(13.94, 0.96) * mm, v(13.93, 0.94) * mm]});
            skFitSpline(sketch, "E213", {"points": [v(13.93, 0.94) * mm, v(13.69, 0.7) * mm, v(13.4, 0.47) * mm, v(13.05, 0.25) * mm]});
            skFitSpline(sketch, "E214", {"points": [v(13.05, 0.25) * mm, v(12.7, 0.05) * mm, v(12.4, -0.11) * mm, v(12.17, -0.22) * mm]});
            skFitSpline(sketch, "E215", {"points": [v(12.17, -0.22) * mm, v(11.95, -0.33) * mm, v(11.82, -0.4) * mm, v(11.8, -0.41) * mm]});
            skFitSpline(sketch, "E216", {"points": [v(11.8, -0.41) * mm, v(11.85, -0.5) * mm, v(12, -0.57) * mm, v(12.24, -0.6) * mm]});
            skFitSpline(sketch, "E217", {"points": [v(12.24, -0.6) * mm, v(12.5, -0.62) * mm, v(12.75, -0.62) * mm, v(13.02, -0.62) * mm]});
            skFitSpline(sketch, "E218", {"points": [v(13.02, -0.62) * mm, v(13.3, -0.6) * mm, v(13.53, -0.6) * mm, v(13.74, -0.58) * mm]});
            skFitSpline(sketch, "E219", {"points": [v(13.74, -0.58) * mm, v(13.96, -0.56) * mm, v(14.07, -0.55) * mm, v(14.07, -0.55) * mm, v(13.74, -0.58) * mm]});
            skLineSegment(sketch, "E220", {"start": v(14.07, -0.55) * mm, "end": v(12.57, -5.9) * mm});
            skFitSpline(sketch, "E221", {"points": [v(21.1, -5.7) * mm, v(21.1, -6.11) * mm, v(21.17, -6.5) * mm, v(21.3, -6.89) * mm]});
            skFitSpline(sketch, "E222", {"points": [v(21.3, -6.89) * mm, v(21.45, -7.27) * mm, v(21.65, -7.6) * mm, v(21.9, -7.88) * mm]});
            skFitSpline(sketch, "E223", {"points": [v(21.9, -7.88) * mm, v(22.17, -8.17) * mm, v(22.48, -8.4) * mm, v(22.83, -8.57) * mm]});
            skFitSpline(sketch, "E224", {"points": [v(22.83, -8.57) * mm, v(23.19, -8.75) * mm, v(23.58, -8.83) * mm, v(24.01, -8.83) * mm]});
            skFitSpline(sketch, "E225", {"points": [v(24.01, -8.83) * mm, v(24.17, -8.83) * mm, v(24.42, -8.76) * mm, v(24.77, -8.62) * mm]});
            skFitSpline(sketch, "E226", {"points": [v(24.77, -8.62) * mm, v(25.13, -8.48) * mm, v(25.53, -8.28) * mm, v(25.96, -8.03) * mm]});
            skFitSpline(sketch, "E227", {"points": [v(25.96, -8.03) * mm, v(26.4, -7.77) * mm, v(26.85, -7.48) * mm, v(27.3, -7.15) * mm]});
            skFitSpline(sketch, "E228", {"points": [v(27.3, -7.15) * mm, v(27.77, -6.82) * mm, v(28.19, -6.45) * mm, v(28.57, -6.06) * mm]});
            skFitSpline(sketch, "E229", {"points": [v(28.57, -6.06) * mm, v(28.95, -5.66) * mm, v(29.25, -5.26) * mm, v(29.5, -4.85) * mm]});
            skFitSpline(sketch, "E230", {"points": [v(29.5, -4.85) * mm, v(29.74, -4.42) * mm, v(29.87, -4) * mm, v(29.87, -3.57) * mm]});
            skFitSpline(sketch, "E231", {"points": [v(29.87, -3.57) * mm, v(29.87, -3.04) * mm, v(29.8, -2.52) * mm, v(29.63, -2) * mm]});
            skFitSpline(sketch, "E232", {"points": [v(29.63, -2) * mm, v(29.48, -1.46) * mm, v(29.24, -0.99) * mm, v(28.92, -0.58) * mm]});
            skFitSpline(sketch, "E233", {"points": [v(28.92, -0.58) * mm, v(28.62, -0.15) * mm, v(28.25, 0.2) * mm, v(27.8, 0.47) * mm]});
            skFitSpline(sketch, "E234", {"points": [v(27.8, 0.47) * mm, v(27.36, 0.74) * mm, v(26.87, 0.87) * mm, v(26.31, 0.87) * mm]});
            skFitSpline(sketch, "E235", {"points": [v(26.31, 0.87) * mm, v(26.19, 0.87) * mm, v(25.93, 0.78) * mm, v(25.53, 0.59) * mm]});
            skFitSpline(sketch, "E236", {"points": [v(25.53, 0.59) * mm, v(25.13, 0.41) * mm, v(24.73, 0.21) * mm, v(24.32, 0) * mm]});
            skFitSpline(sketch, "E237", {"points": [v(24.32, 0) * mm, v(23.92, -0.21) * mm, v(23.6, -0.4) * mm, v(23.32, -0.55) * mm]});
            skFitSpline(sketch, "E238", {"points": [v(23.32, -0.55) * mm, v(23.07, -0.7) * mm, v(23.02, -0.74) * mm, v(23.16, -0.7) * mm]});
            skFitSpline(sketch, "E239", {"points": [v(23.16, -0.7) * mm, v(23.52, -0.57) * mm, v(23.86, -0.52) * mm, v(24.18, -0.55) * mm]});
            skFitSpline(sketch, "E240", {"points": [v(24.18, -0.55) * mm, v(24.51, -0.57) * mm, v(24.76, -0.6) * mm, v(24.94, -0.67) * mm]});
            skFitSpline(sketch, "E241", {"points": [v(24.94, -0.67) * mm, v(25.11, -0.74) * mm, v(25.2, -0.77) * mm, v(25.22, -0.8) * mm]});
            skFitSpline(sketch, "E242", {"points": [v(25.22, -0.8) * mm, v(25.2, -0.8) * mm, v(25.09, -0.85) * mm, v(24.87, -0.96) * mm]});
            skFitSpline(sketch, "E243", {"points": [v(24.87, -0.96) * mm, v(24.66, -1.07) * mm, v(24.4, -1.23) * mm, v(24.08, -1.43) * mm]});
            skFitSpline(sketch, "E244", {"points": [v(24.08, -1.43) * mm, v(23.78, -1.64) * mm, v(23.46, -1.89) * mm, v(23.11, -2.2) * mm]});
            skFitSpline(sketch, "E245", {"points": [v(23.11, -2.2) * mm, v(22.76, -2.47) * mm, v(22.44, -2.8) * mm, v(22.14, -3.16) * mm]});
            skFitSpline(sketch, "E246", {"points": [v(22.14, -3.16) * mm, v(21.84, -3.53) * mm, v(21.58, -3.92) * mm, v(21.38, -4.35) * mm]});
            skFitSpline(sketch, "E247", {"points": [v(21.38, -4.35) * mm, v(21.19, -4.78) * mm, v(21.1, -5.23) * mm, v(21.1, -5.7) * mm]});
            skFitSpline(sketch, "E248", {"points": [v(25.7, -7.86) * mm, v(25.65, -7.86) * mm, v(25.5, -7.78) * mm, v(25.22, -7.62) * mm]});
            skFitSpline(sketch, "E249", {"points": [v(25.22, -7.62) * mm, v(24.95, -7.46) * mm, v(24.66, -7.24) * mm, v(24.34, -6.93) * mm]});
            skFitSpline(sketch, "E250", {"points": [v(24.34, -6.93) * mm, v(24.04, -6.62) * mm, v(23.77, -6.25) * mm, v(23.51, -5.82) * mm]});
            skFitSpline(sketch, "E251", {"points": [v(23.51, -5.82) * mm, v(23.28, -5.38) * mm, v(23.16, -4.87) * mm, v(23.16, -4.3) * mm]});
            skFitSpline(sketch, "E252", {"points": [v(23.16, -4.3) * mm, v(23.16, -3.78) * mm, v(23.26, -3.31) * mm, v(23.47, -2.9) * mm]});
            skFitSpline(sketch, "E253", {"points": [v(23.47, -2.9) * mm, v(23.67, -2.47) * mm, v(23.9, -2.12) * mm, v(24.18, -1.83) * mm]});
            skFitSpline(sketch, "E254", {"points": [v(24.18, -1.83) * mm, v(24.45, -1.53) * mm, v(24.7, -1.3) * mm, v(24.96, -1.15) * mm]});
            skFitSpline(sketch, "E255", {"points": [v(24.96, -1.15) * mm, v(25.21, -0.99) * mm, v(25.39, -0.9) * mm, v(25.48, -0.9) * mm]});
            skFitSpline(sketch, "E256", {"points": [v(25.48, -0.9) * mm, v(25.56, -0.9) * mm, v(25.73, -1.04) * mm, v(25.98, -1.29) * mm]});
            skFitSpline(sketch, "E257", {"points": [v(25.98, -1.29) * mm, v(26.25, -1.53) * mm, v(26.52, -1.83) * mm, v(26.79, -2.21) * mm]});
            skFitSpline(sketch, "E258", {"points": [v(26.79, -2.21) * mm, v(27.07, -2.6) * mm, v(27.32, -3.02) * mm, v(27.52, -3.5) * mm]});
            skFitSpline(sketch, "E259", {"points": [v(27.52, -3.5) * mm, v(27.74, -3.97) * mm, v(27.85, -4.44) * mm, v(27.85, -4.9) * mm]});
            skFitSpline(sketch, "E260", {"points": [v(27.85, -4.9) * mm, v(27.85, -5.4) * mm, v(27.75, -5.84) * mm, v(27.55, -6.2) * mm]});
            skFitSpline(sketch, "E261", {"points": [v(27.55, -6.2) * mm, v(27.34, -6.56) * mm, v(27.1, -6.87) * mm, v(26.83, -7.12) * mm]});
            skFitSpline(sketch, "E262", {"points": [v(26.83, -7.12) * mm, v(26.58, -7.38) * mm, v(26.34, -7.57) * mm, v(26.1, -7.7) * mm]});
            skFitSpline(sketch, "E263", {"points": [v(26.1, -7.7) * mm, v(25.88, -7.8) * mm, v(25.74, -7.86) * mm, v(25.7, -7.86) * mm]});
            skFitSpline(sketch, "E264", {"points": [v(31.27, -8.8) * mm, v(31.73, -8.52) * mm, v(32.14, -8.22) * mm, v(32.5, -7.88) * mm]});
            skFitSpline(sketch, "E265", {"points": [v(32.5, -7.88) * mm, v(32.87, -7.55) * mm, v(33.18, -7.3) * mm, v(33.45, -7.1) * mm]});
            skFitSpline(sketch, "E266", {"points": [v(33.45, -7.1) * mm, v(33.45, -7.1) * mm, v(33.48, -7.01) * mm, v(33.55, -6.84) * mm, v(33.45, -7.1) * mm]});
            skFitSpline(sketch, "E267", {"points": [v(33.55, -6.84) * mm, v(33.63, -6.67) * mm, v(33.7, -6.48) * mm, v(33.78, -6.27) * mm]});
            skFitSpline(sketch, "E268", {"points": [v(33.78, -6.27) * mm, v(33.86, -6.05) * mm, v(33.93, -5.85) * mm, v(34, -5.68) * mm]});
            skFitSpline(sketch, "E269", {"points": [v(34, -5.68) * mm, v(34.06, -5.5) * mm, v(34.1, -5.42) * mm, v(34.1, -5.42) * mm, v(34, -5.68) * mm]});
            skFitSpline(sketch, "E270", {"points": [v(34.1, -5.42) * mm, v(34.28, -5.07) * mm, v(34.56, -4.64) * mm, v(34.92, -4.14) * mm]});
            skFitSpline(sketch, "E271", {"points": [v(34.92, -4.14) * mm, v(35.29, -3.63) * mm, v(35.67, -3.15) * mm, v(36.06, -2.69) * mm]});
            skFitSpline(sketch, "E272", {"points": [v(36.06, -2.69) * mm, v(36.47, -2.23) * mm, v(36.87, -1.84) * mm, v(37.25, -1.53) * mm]});
            skFitSpline(sketch, "E273", {"points": [v(37.25, -1.53) * mm, v(37.64, -1.2) * mm, v(37.96, -1.06) * mm, v(38.2, -1.08) * mm]});
            skFitSpline(sketch, "E274", {"points": [v(38.2, -1.08) * mm, v(38.39, -1.1) * mm, v(38.62, -1.06) * mm, v(38.9, -0.98) * mm]});
            skFitSpline(sketch, "E275", {"points": [v(38.9, -0.98) * mm, v(39.2, -0.9) * mm, v(39.52, -0.8) * mm, v(39.86, -0.67) * mm]});
            skFitSpline(sketch, "E276", {"points": [v(39.86, -0.67) * mm, v(40.19, -0.53) * mm, v(40.53, -0.37) * mm, v(40.88, -0.2) * mm]});
            skFitSpline(sketch, "E277", {"points": [v(40.88, -0.2) * mm, v(41.22, 0) * mm, v(41.55, 0.19) * mm, v(41.85, 0.4) * mm]});
            skFitSpline(sketch, "E278", {"points": [v(41.85, 0.4) * mm, v(41.82, 0.4) * mm, v(41.68, 0.4) * mm, v(41.42, 0.4) * mm]});
            skFitSpline(sketch, "E279", {"points": [v(41.42, 0.4) * mm, v(41.17, 0.4) * mm, v(40.84, 0.42) * mm, v(40.45, 0.47) * mm]});
            skFitSpline(sketch, "E280", {"points": [v(40.45, 0.47) * mm, v(40.07, 0.51) * mm, v(39.74, 0.62) * mm, v(39.45, 0.78) * mm]});
            skFitSpline(sketch, "E281", {"points": [v(39.45, 0.78) * mm, v(39.37, 0.8) * mm, v(39.15, 0.7) * mm, v(38.79, 0.44) * mm]});
            skFitSpline(sketch, "E282", {"points": [v(38.79, 0.44) * mm, v(38.44, 0.2) * mm, v(38.02, -0.14) * mm, v(37.53, -0.6) * mm]});
            skFitSpline(sketch, "E283", {"points": [v(37.53, -0.6) * mm, v(37.06, -1.04) * mm, v(36.54, -1.57) * mm, v(35.99, -2.17) * mm]});
            skFitSpline(sketch, "E284", {"points": [v(35.99, -2.17) * mm, v(35.45, -2.77) * mm, v(34.96, -3.4) * mm, v(34.52, -4.06) * mm]});
            skFitSpline(sketch, "E285", {"points": [v(34.52, -4.06) * mm, v(34.52, -4.06) * mm, v(34.57, -3.94) * mm, v(34.66, -3.68) * mm, v(34.52, -4.06) * mm]});
            skFitSpline(sketch, "E286", {"points": [v(34.66, -3.68) * mm, v(34.77, -3.42) * mm, v(34.9, -3.08) * mm, v(35.04, -2.69) * mm]});
            skFitSpline(sketch, "E287", {"points": [v(35.04, -2.69) * mm, v(35.2, -2.28) * mm, v(35.36, -1.83) * mm, v(35.52, -1.36) * mm]});
            skFitSpline(sketch, "E288", {"points": [v(35.52, -1.36) * mm, v(35.67, -0.89) * mm, v(35.8, -0.44) * mm, v(35.9, -0.03) * mm]});
            skFitSpline(sketch, "E289", {"points": [v(35.9, -0.03) * mm, v(35.91, 0.06) * mm, v(35.97, 0.17) * mm, v(36.06, 0.28) * mm]});
            skFitSpline(sketch, "E290", {"points": [v(36.06, 0.28) * mm, v(36.16, 0.39) * mm, v(36.24, 0.5) * mm, v(36.32, 0.59) * mm]});
            skFitSpline(sketch, "E291", {"points": [v(36.32, 0.59) * mm, v(36.4, 0.68) * mm, v(36.46, 0.75) * mm, v(36.49, 0.8) * mm]});
            skFitSpline(sketch, "E292", {"points": [v(36.49, 0.8) * mm, v(36.54, 0.85) * mm, v(36.51, 0.85) * mm, v(36.42, 0.82) * mm]});
            skFitSpline(sketch, "E293", {"points": [v(36.42, 0.82) * mm, v(36, 0.68) * mm, v(35.62, 0.57) * mm, v(35.25, 0.5) * mm]});
            skFitSpline(sketch, "E294", {"points": [v(35.25, 0.5) * mm, v(34.9, 0.43) * mm, v(34.57, 0.38) * mm, v(34.28, 0.35) * mm]});
            skFitSpline(sketch, "E295", {"points": [v(34.28, 0.35) * mm, v(34, 0.32) * mm, v(33.77, 0.3) * mm, v(33.6, 0.3) * mm]});
            skFitSpline(sketch, "E296", {"points": [v(33.6, 0.3) * mm, v(33.44, 0.3) * mm, v(33.36, 0.3) * mm, v(33.36, 0.3) * mm, v(33.6, 0.3) * mm]});
            skFitSpline(sketch, "E297", {"points": [v(33.36, 0.3) * mm, v(33.12, -1.42) * mm, v(32.87, -2.88) * mm, v(32.6, -4.06) * mm]});
            skFitSpline(sketch, "E298", {"points": [v(32.6, -4.06) * mm, v(32.33, -5.23) * mm, v(32.08, -6.18) * mm, v(31.86, -6.91) * mm]});
            skFitSpline(sketch, "E299", {"points": [v(31.86, -6.91) * mm, v(31.64, -7.62) * mm, v(31.47, -8.13) * mm, v(31.34, -8.43) * mm]});
            skFitSpline(sketch, "E300", {"points": [v(31.34, -8.43) * mm, v(31.23, -8.71) * mm, v(31.2, -8.84) * mm, v(31.27, -8.8) * mm]});
            skSolve(sketch);
        }
        {
            var Q0;
            Q0=makeQuery(id+"F0.imprint","IMPRINT",FACE,{"disambiguationData":[TD([[makeQuery(id+"F0.imprint","IMPRINT",EDGE,{"derivedFrom":sQuery(id+"F0.wireOp",EDGE,"E0")}),-1.0]])]});
            extrude(context, id + "F1", {"entities" : qUnion([Q0]), "depth" : 0.4 * mm, "offsetDistance" : 25 * mm});
        }
    });
